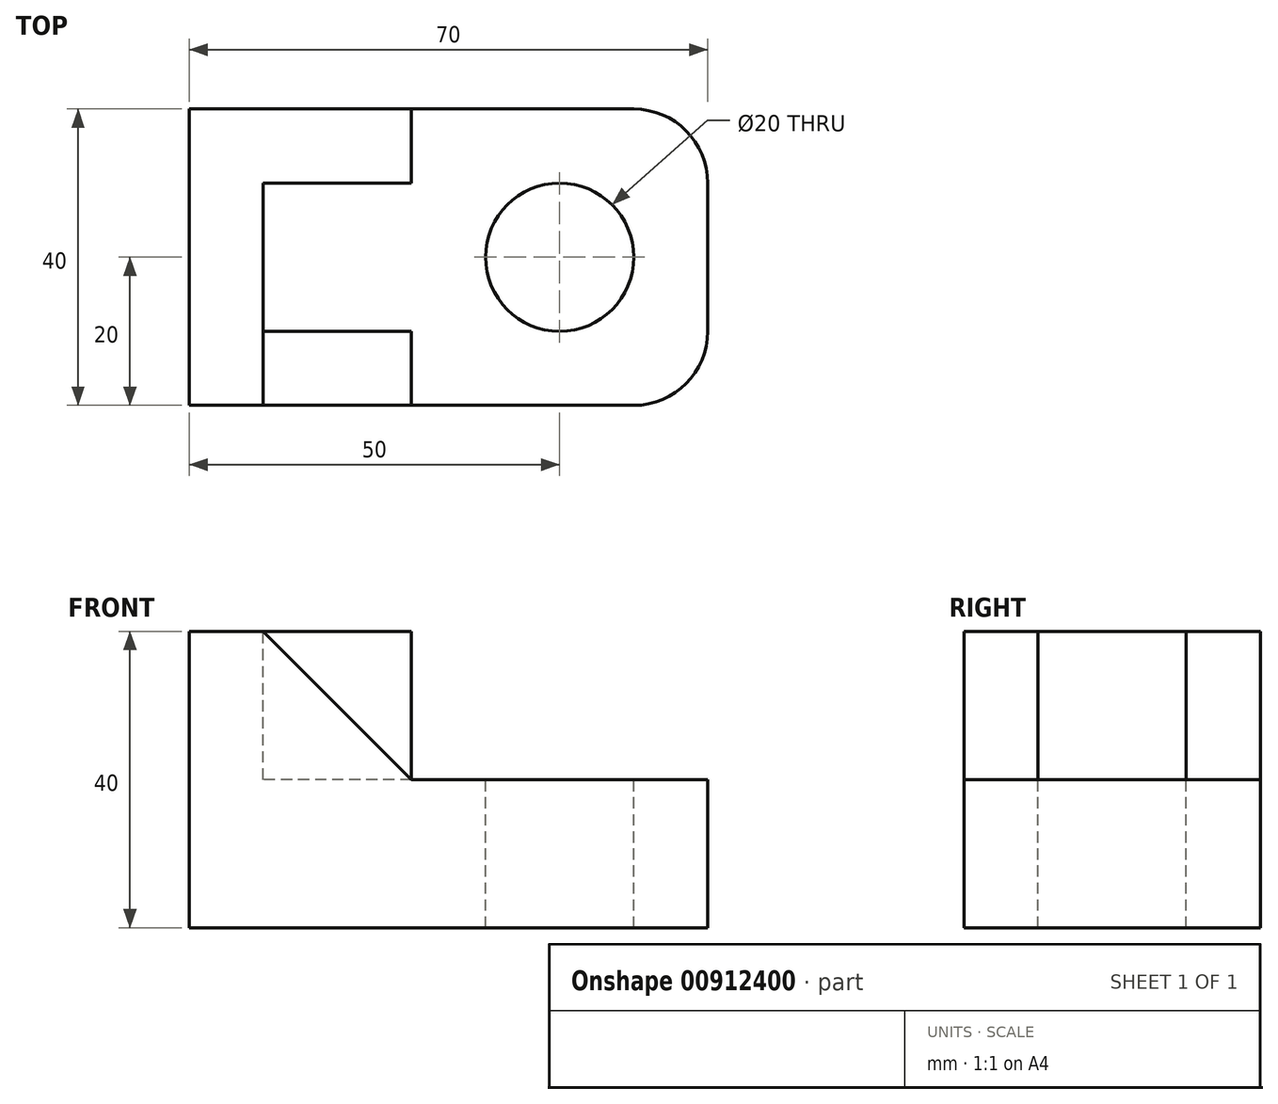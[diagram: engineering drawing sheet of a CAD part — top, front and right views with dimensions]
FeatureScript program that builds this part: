
annotation { "Feature Type Name" : "Feature", "Feature Type Description" : "" }
export const myFeature = defineFeature(function(context is Context, id is Id, definition is map)
    precondition{}
    {
        {
            var Q0;
            Q0=qCreatedBy(makeId("Top.planeOp"),FACE);
            var sketch = newSketch(context, id + "F0", { "sketchPlane" : qUnion([Q0])});
            skLineSegment(sketch, "E0.bottom", {"start": v(0, 0) * mm, "end": v(60, 0) * mm});
            skLineSegment(sketch, "E0.top", {"start": v(0, 40) * mm, "end": v(60, 40) * mm});
            skLineSegment(sketch, "E0.left", {"start": v(0, 0) * mm, "end": v(0, 40) * mm});
            skLineSegment(sketch, "E0.right", {"start": v(70, 10) * mm, "end": v(70, 30) * mm});
            skPoint(sketch, "E1.visualSharp", {"position": v(70, 40) * mm});
            skArc(sketch, "E1.filletArc", {"start": v(70, 30) * mm, "mid": v(67.07, 37.07) * mm, "end": v(60, 40) * mm});
            skPoint(sketch, "E2.visualSharp", {"position": v(70, 0) * mm});
            skArc(sketch, "E2.filletArc", {"start": v(60, 0) * mm, "mid": v(67.07, 2.93) * mm, "end": v(70, 10) * mm});
            skSolve(sketch);
        }
        {
            var Q0;
            Q0=makeQuery(id+"F0.imprint","IMPRINT",FACE,{"disambiguationData":[TD([[makeQuery(id+"F0.imprint","IMPRINT",EDGE,{"derivedFrom":sQuery(id+"F0.wireOp",EDGE,"E0.bottom")}),1.0]])]});
            extrude(context, id + "F1", {"entities" : qUnion([Q0]), "depth" : 40 * mm, "offsetDistance" : 25 * mm});
        }
        {
            var Q0;
            Q0=makeQuery(id+"F1.opExtrude","CAP_FACE",FACE,{"disambiguationData":[OSD([sQuery(id+"F0.wireOp",EDGE,"E0.bottom"),sQuery(id+"F0.wireOp",EDGE,"E0.top"),sQuery(id+"F0.wireOp",EDGE,"E0.left"),sQuery(id+"F0.wireOp",EDGE,"E0.right"),sQuery(id+"F0.wireOp",EDGE,"E1.filletArc"),sQuery(id+"F0.wireOp",EDGE,"E2.filletArc")])],"isStart":false});
            var sketch = newSketch(context, id + "F2", { "sketchPlane" : qUnion([Q0])});
            skLineSegment(sketch, "E3", {"start": v(0, 20) * mm, "end": v(70, 20) * mm, "construction": true});
            skCircle(sketch, "E4", {"center": v(50, 20) * mm, "radius": 10 * mm});
            skLineSegment(sketch, "E5", {"start": v(30, 40) * mm, "end": v(30, 30) * mm});
            skLineSegment(sketch, "E6", {"start": v(30, 30) * mm, "end": v(10, 30) * mm});
            skLineSegment(sketch, "E7", {"start": v(10, 30) * mm, "end": v(10, 10) * mm});
            skLineSegment(sketch, "E8", {"start": v(10, 10) * mm, "end": v(30, 10) * mm});
            skLineSegment(sketch, "E9", {"start": v(30, 10) * mm, "end": v(30, 0) * mm});
            skLineSegment(sketch, "E10.0", {"start": v(0, 40) * mm, "end": v(60, 40) * mm});
            skLineSegment(sketch, "E11.0", {"start": v(0, 0) * mm, "end": v(0, 40) * mm});
            skLineSegment(sketch, "E12.0", {"start": v(0, 0) * mm, "end": v(60, 0) * mm});
            skSolve(sketch);
        }
        {
            var Q0;
            Q0=makeQuery(id+"F2.imprint","IMPRINT",FACE,{"disambiguationData":[TD([[makeQuery(id+"F2.imprint","IMPRINT",EDGE,{"derivedFrom":sQuery(id+"F2.wireOp",EDGE,"E4")}),-1.0]])]});
            extrude(context, id + "F3", {"entities" : qUnion([Q0]), "operationType" : NewBodyOperationType.REMOVE, "oppositeDirection" : true, "depth" : 20 * mm, "offsetDistance" : 25 * mm});
        }
        {
            var Q0;
            Q0=makeQuery(id+"F3.boolean.opBoolean","SPLIT",FACE,{"disambiguationData":[TD([makeQuery(id+"F3.opExtrude","SWEPT_FACE",FACE,{"disambiguationData":[OSD([sQuery(id+"F2.wireOp",EDGE,"E4")])]})])],"derivedFrom":makeQuery(id+"F1.opExtrude","CAP_FACE",FACE,{"disambiguationData":[OSD([sQuery(id+"F0.wireOp",EDGE,"E0.bottom"),sQuery(id+"F0.wireOp",EDGE,"E0.top"),sQuery(id+"F0.wireOp",EDGE,"E0.left"),sQuery(id+"F0.wireOp",EDGE,"E0.right"),sQuery(id+"F0.wireOp",EDGE,"E1.filletArc"),sQuery(id+"F0.wireOp",EDGE,"E2.filletArc")])],"isStart":false})});
            extrude(context, id + "F4", {"entities" : qUnion([Q0]), "operationType" : NewBodyOperationType.REMOVE, "endBound" : BoundingType.THROUGH_ALL, "oppositeDirection" : true, "depth" : 25 * mm, "offsetDistance" : 25 * mm});
        }
        {
            var Q0;
            Q0=makeQuery(id+"F3.boolean.opBoolean","COPY",FACE,{"derivedFrom":makeQuery(id+"F3.opExtrude","SWEPT_FACE",FACE,{"disambiguationData":[OSD([sQuery(id+"F2.wireOp",EDGE,"E8")])]})});
            var sketch = newSketch(context, id + "F5", { "sketchPlane" : qUnion([Q0])});
            skLineSegment(sketch, "E13.0", {"start": v(-10, 40) * mm, "end": v(-30, 40) * mm});
            skLineSegment(sketch, "E14.0", {"start": v(-30, 20) * mm, "end": v(-30, 40) * mm});
            skLineSegment(sketch, "E15", {"start": v(-10, 40) * mm, "end": v(-30, 20) * mm});
            skSolve(sketch);
        }
        {
            var Q0;
            Q0=makeQuery(id+"F5.imprint","IMPRINT",FACE,{"disambiguationData":[TD([[makeQuery(id+"F5.imprint","IMPRINT",EDGE,{"derivedFrom":sQuery(id+"F5.wireOp",EDGE,"E13.0")}),1.0]])]});
            extrude(context, id + "F6", {"entities" : qUnion([Q0]), "operationType" : NewBodyOperationType.REMOVE, "endBound" : BoundingType.THROUGH_ALL, "oppositeDirection" : true, "depth" : 25 * mm, "offsetDistance" : 25 * mm});
        }
    });
